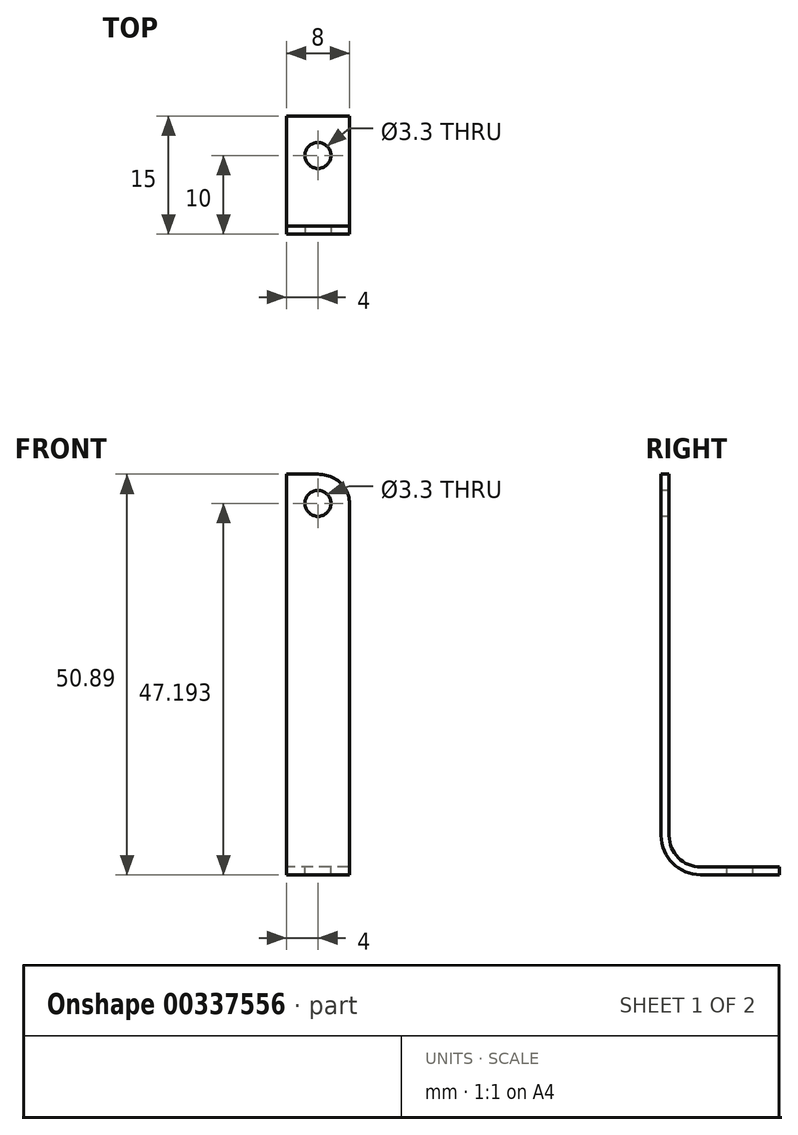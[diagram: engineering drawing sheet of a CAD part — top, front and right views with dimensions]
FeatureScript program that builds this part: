
annotation { "Feature Type Name" : "Feature", "Feature Type Description" : "" }
export const myFeature = defineFeature(function(context is Context, id is Id, definition is map)
    precondition{}
    {
        {
            var Q0;
            Q0=qCreatedBy(makeId("Right.planeOp"),FACE);
            var sketch = newSketch(context, id + "F0", { "sketchPlane" : qUnion([Q0])});
            skLineSegment(sketch, "E0", {"start": v(15, 0) * mm, "end": v(5, 0) * mm});
            skLineSegment(sketch, "E1", {"start": v(0, 5) * mm, "end": v(0, 50.9) * mm});
            skPoint(sketch, "E2.visualSharp", {"position": v(0, 0) * mm});
            skArc(sketch, "E2.filletArc", {"start": v(0, 5) * mm, "mid": v(1.46, 1.46) * mm, "end": v(5, 0) * mm});
            skSolve(sketch);
        }
        {
            var Q0;
            Q0=sQuery(id+"F0.wireOp",VERTEX,"E0.start");
            var Q1;
            Q1=sQuery(id+"F0.wireOp",EDGE,"E0");
            cPlane(context, id + "F1", {"entities" : qUnion([Q0, Q1]), "cplaneType" : CPlaneType.LINE_POINT, "offset" : 25 * mm, "width" : 150 * mm, "height" : 150 * mm});
        }
        {
            var Q0;
            Q0=qCreatedBy(id+"F1.planeOp",FACE);
            var sketch = newSketch(context, id + "F2", { "sketchPlane" : qUnion([Q0])});
            skLineSegment(sketch, "E3.bottom", {"start": v(0, 0) * mm, "end": v(-8, 0) * mm});
            skLineSegment(sketch, "E3.top", {"start": v(0, 1) * mm, "end": v(-8, 1) * mm});
            skLineSegment(sketch, "E3.left", {"start": v(0, 0) * mm, "end": v(0, 1) * mm});
            skLineSegment(sketch, "E3.right", {"start": v(-8, 0) * mm, "end": v(-8, 1) * mm});
            skSolve(sketch);
        }
        {
            var Q0;
            Q0 = qSketchRegion(id + "F2", true);
            var Q1;
            Q1 = qConstructionFilter(qBodyType(qCreatedBy(id + "F0" ,EDGE), BodyType.WIRE), ConstructionObject.NO);
            sweep(context, id + "F3", {"profiles" : qUnion([Q0]), "path" : qUnion([Q1])});
        }
        {
            var Q0;
            Q0=makeQuery(id+"F3.opSweep","SWEPT_FACE",FACE,{"disambiguationData":[OSD([sQuery(id+"F0.wireOp",EDGE,"E0"),sQuery(id+"F2.wireOp",EDGE,"E3.top")])]});
            var sketch = newSketch(context, id + "F4", { "sketchPlane" : qUnion([Q0])});
            skLineSegment(sketch, "E4", {"start": v(-8, 5) * mm, "end": v(0, 15) * mm, "construction": true});
            skLineSegment(sketch, "E5", {"start": v(-8, 15) * mm, "end": v(0, 5) * mm, "construction": true});
            skCircle(sketch, "E6", {"center": v(-4, 10) * mm, "radius": 3.58 * mm, "construction": true});
            skSolve(sketch);
        }
        {
            var Q0;
            Q0=sQuery(id+"F4.wireOp",VERTEX,"E6.center");
            var Q1;
            Q1=makeQuery(id+"F3.opSweep","SWEPT_BODY",BODY,{"disambiguationData":[OSD([sQuery(id+"F0.wireOp",EDGE,"E0"),sQuery(id+"F2.wireOp",EDGE,"E3.bottom"),sQuery(id+"F2.wireOp",EDGE,"E3.top"),sQuery(id+"F2.wireOp",EDGE,"E3.left"),sQuery(id+"F2.wireOp",EDGE,"E3.right")])]});
            hole(context, id + "F5", {"style" : HoleStyle.SIMPLE, "endStyle" : HoleEndStyle.THROUGH, "standardTappedOrClearance" : lookupTablePath({ "standard" : "ISO", "fit" : "Normal", "size" : "M3", "type" : "Clearance" }), "standardBlindInLast" : lookupTablePath({ "fit" : "Standard", "standard" : "ISO", "size" : "M3", "type" : "Clearance" }), "holeDiameter" : 3.3 * mm, "isTappedThrough" : true, "tappedDepth" : 12 * mm, "tapClearance" : 3, "locations" : qUnion([Q0]), "scope" : qUnion([Q1])});
        }
        {
            var Q0;
            Q0=makeQuery(id+"F3.opSweep","SWEPT_FACE",FACE,{"disambiguationData":[OSD([sQuery(id+"F0.wireOp",EDGE,"E1"),sQuery(id+"F2.wireOp",EDGE,"E3.bottom")])]});
            var sketch = newSketch(context, id + "F6", { "sketchPlane" : qUnion([Q0])});
            skLineSegment(sketch, "E7", {"start": v(-4, 50.9) * mm, "end": v(-4, 22.1) * mm, "construction": true});
            skCircle(sketch, "E8", {"center": v(-4, 47.2) * mm, "radius": 1.65 * mm, "construction": true});
            skCircle(sketch, "E9", {"center": v(-4, 47.2) * mm, "radius": 3.9 * mm, "construction": true});
            skSolve(sketch);
        }
        {
            var Q0;
            Q0=sQuery(id+"F6.wireOp",VERTEX,"E8.center");
            var Q1;
            Q1=makeQuery(id+"F3.opSweep","SWEPT_BODY",BODY,{"disambiguationData":[OSD([sQuery(id+"F0.wireOp",EDGE,"E0"),sQuery(id+"F2.wireOp",EDGE,"E3.bottom"),sQuery(id+"F2.wireOp",EDGE,"E3.top"),sQuery(id+"F2.wireOp",EDGE,"E3.left"),sQuery(id+"F2.wireOp",EDGE,"E3.right")])]});
            hole(context, id + "F7", {"style" : HoleStyle.SIMPLE, "endStyle" : HoleEndStyle.THROUGH, "standardTappedOrClearance" : lookupTablePath({ "standard" : "ISO", "fit" : "Normal", "size" : "M3", "type" : "Clearance" }), "standardBlindInLast" : lookupTablePath({ "fit" : "Standard", "standard" : "ISO", "size" : "M3", "type" : "Clearance" }), "holeDiameter" : 3.3 * mm, "isTappedThrough" : true, "tappedDepth" : 12 * mm, "tapClearance" : 3, "locations" : qUnion([Q0]), "scope" : qUnion([Q1])});
        }
        {
            var Q0;
            Q0=makeQuery(id+"F3.opSweep","SWEPT_FACE",FACE,{"disambiguationData":[OSD([sQuery(id+"F0.wireOp",EDGE,"E1"),sQuery(id+"F2.wireOp",EDGE,"E3.bottom")])]});
            var sketch = newSketch(context, id + "F8", { "sketchPlane" : qUnion([Q0])});
            skPoint(sketch, "E10.0", {"position": v(-4, 47.2) * mm});
            skEllipticalArc(sketch, "E11", {});
            skLineSegment(sketch, "E12.bottom", {"start": v(0, 50.9) * mm, "end": v(-4, 50.9) * mm});
            skLineSegment(sketch, "E12.left", {"start": v(0, 50.9) * mm, "end": v(0, 47.2) * mm});
            const initialGuessF8  = {"E11": [-0.004, 0.04719342594146728, 1, 0, 0.004, 0.0037, 0, 1.5707963267948966]};
            skSetInitialGuess(sketch, initialGuessF8);
            skSolve(sketch);
        }
        {
            var Q0;
            Q0 = qSketchRegion(id + "F8", true);
            extrude(context, id + "F9", {"entities" : qUnion([Q0]), "operationType" : NewBodyOperationType.REMOVE, "endBound" : BoundingType.THROUGH_ALL, "oppositeDirection" : true, "depth" : 25 * mm});
        }
    });
